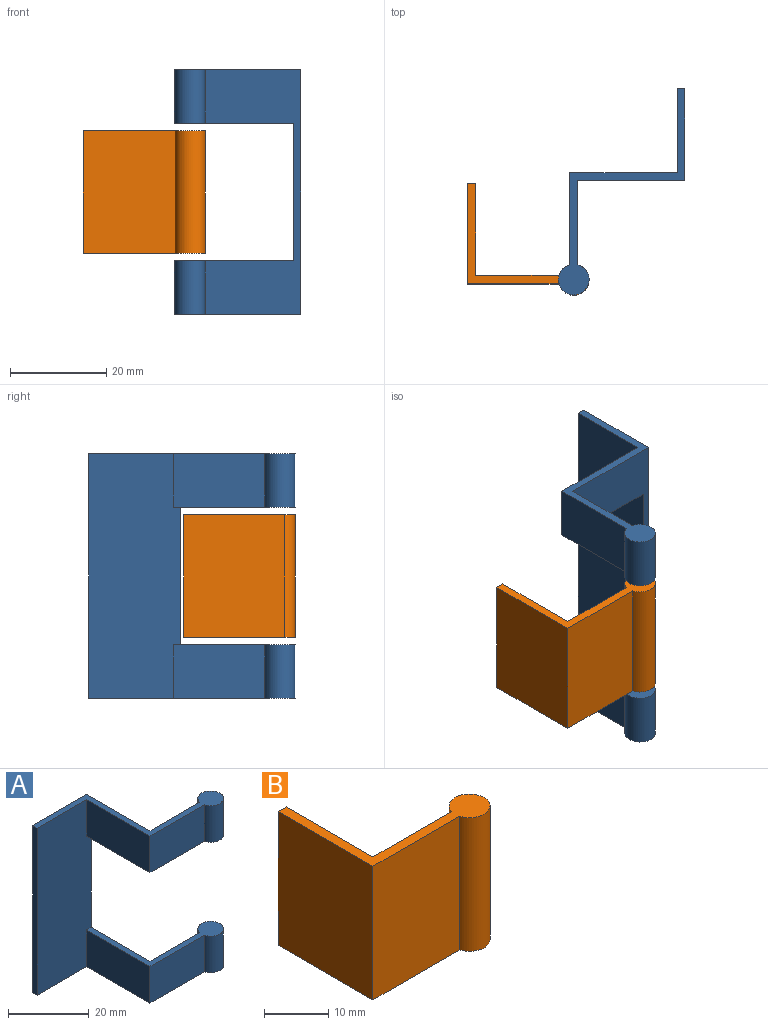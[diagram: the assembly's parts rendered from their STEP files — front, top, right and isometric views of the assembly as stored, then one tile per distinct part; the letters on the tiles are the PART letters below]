
ASSEMBLY  parts=2 mates=1
PART A: 16 faces, bbox 42.8x26.2x50.8 mm
  f0: plane 19.05x11.11mm, normal (0,-1,0), area 211.7mm2, adj f1,f4,f12,f14
  f1: cylinder r=3.17mm len=11.11mm, axis (0,0,-1), area 203.9mm2, adj f0,f2,f12,f14
  f2: plane 17.46x11.11mm, normal (0,1,0), area 194.1mm2, adj f1,f3,f12,f14
  f3: plane 50.8x22.23mm, normal (1,0,0), area 539.3mm2, adj f2,f7,f8,f10,f12,f13,f14,f15
  f4: plane 22.23x11.11mm, normal (-1,0,0), area 247mm2, adj f0,f10,f12,f14
  f5: plane 19.05x11.11mm, normal (0,-1,0), area 211.7mm2, adj f6,f11,f13,f15
  f6: cylinder r=3.17mm len=11.11mm, axis (0,0,-1), area 203.9mm2, adj f5,f7,f13,f15
  f7: plane 17.46x11.11mm, normal (0,1,0), area 194.1mm2, adj f3,f6,f13,f15
  f8: plane 50.8x19.05mm, normal (0,1,0), area 967.7mm2, adj f3,f9,f12,f13
  f9: plane 50.8x1.59mm, normal (-1,0,0), area 80.6mm2, adj f8,f10,f12,f13
  f10: plane 50.8x19.05mm, normal (0,-1,0), area 932.5mm2, adj f3,f4,f9,f11,f12,f13,f14,f15
  f11: plane 22.23x11.11mm, normal (-1,0,0), area 247mm2, adj f5,f10,f13,f15
  f12: plane 42.76x26.19mm, normal (0,0,1), area 124.8mm2, adj f0,f1,f2,f3,f4,f8,f9,f10
  f13: plane 42.76x26.19mm, normal (0,0,-1), area 124.8mm2, adj f3,f5,f6,f7,f8,f9,f10,f11
  f14: plane 25.3x24.61mm, normal (0,0,-1), area 94.6mm2, adj f0,f1,f2,f3,f4,f10
  f15: plane 25.3x24.61mm, normal (0,0,1), area 94.6mm2, adj f3,f5,f6,f7,f10,f11
PART B: 8 faces, bbox 25.3x23.1x25.4 mm
  f0: plane 25.4x1.78mm, normal (0,1,0), area 45.2mm2, adj f1,f5,f6,f7
  f1: plane 25.4x20.83mm, normal (-1,0,0), area 529mm2, adj f0,f2,f6,f7
  f2: plane 25.4x19.05mm, normal (0,-1,0), area 483.9mm2, adj f1,f3,f6,f7
  f3: cylinder r=3.17mm len=25.4mm, axis (0,0,-1), area 460.9mm2, adj f2,f4,f6,f7
  f4: plane 25.4x17.27mm, normal (0,1,0), area 438.7mm2, adj f3,f5,f6,f7
  f5: plane 25.4x19.05mm, normal (1,0,0), area 483.9mm2, adj f0,f4,f6,f7
  f6: plane 25.27x23.11mm, normal (0,0,1), area 99.3mm2, adj f0,f1,f2,f3,f4,f5
  f7: plane 25.27x23.11mm, normal (0,0,-1), area 99.3mm2, adj f0,f1,f2,f3,f4,f5
PLACE A rot(axis=(0,0,-1),90deg) t=(71.91,23.01,0)mm
PLACE B at identity fixed
MATE revolute B.f3 <-> A.f1  axis (0,0,-1) through (22.1,0.89,12.7)mm
